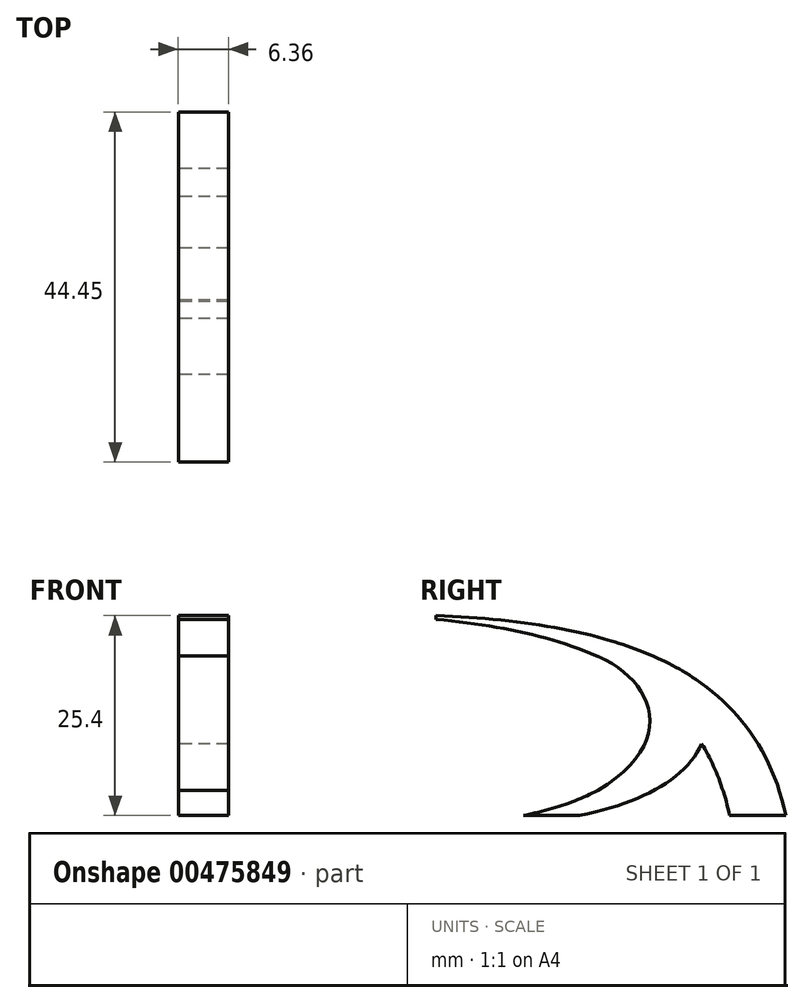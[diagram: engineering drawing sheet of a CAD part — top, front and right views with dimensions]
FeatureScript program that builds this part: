
annotation { "Feature Type Name" : "Feature", "Feature Type Description" : "" }
export const myFeature = defineFeature(function(context is Context, id is Id, definition is map)
    precondition{}
    {
        {
            var Q0;
            Q0=qCreatedBy(makeId("Right.planeOp"),FACE);
            var sketch = newSketch(context, id + "F0", { "sketchPlane" : qUnion([Q0])});
            skFitSpline(sketch, "E0", {"points": [v(226.4, -123.17) * mm, v(-307, 181.63) * mm], "startDerivative": vector(-152.15, 697.22) * mm, "endDerivative": vector(-800.1, 34.28) * mm});
            skFitSpline(sketch, "E1", {"points": [v(-40.3, 143.24) * mm, v(-173.65, -123.17) * mm], "startDerivative": vector(386.18, -408.72) * mm, "endDerivative": vector(-505.78, -101) * mm});
            skFitSpline(sketch, "E2", {"points": [v(45.43, 143.24) * mm, v(-87.92, -123.17) * mm], "startDerivative": vector(386.18, -408.72) * mm, "endDerivative": vector(-505.78, -101) * mm});
            skFitSpline(sketch, "E3", {"points": [v(140.68, -123.17) * mm, v(-392.72, 181.63) * mm], "startDerivative": vector(-152.15, 697.22) * mm, "endDerivative": vector(-800.1, 34.28) * mm});
            skFitSpline(sketch, "E4", {"points": [v(-62.31, 120.1) * mm, v(-60.29, -84.74) * mm], "startDerivative": vector(258.37, -104.87) * mm, "endDerivative": vector(-378.53, -222.19) * mm});
            skLineSegment(sketch, "E5", {"start": v(-307, 181.63) * mm, "end": v(-307, 175.93) * mm});
            skLineSegment(sketch, "E6", {"start": v(-173.65, -123.17) * mm, "end": v(-87.92, -123.17) * mm});
            skLineSegment(sketch, "E7", {"start": v(140.68, -123.17) * mm, "end": v(226.4, -123.17) * mm});
            skSolve(sketch);
        }
        {
            var Q0;
            {var subQ0=sQuery(id+"F0.wireOp",EDGE,"E1");var subQ1=sQuery(id+"F0.wireOp",EDGE,"E0");var subQ2=makeQuery(id+"F0.imprint","INTERSECT",VERTEX,{"derivedFrom":[subQ1,subQ0]});Q0=makeQuery(id+"F0.imprint","IMPRINT",FACE,{"disambiguationData":[TD([[makeQuery(id+"F0.imprint","IMPRINT",EDGE,{"disambiguationData":[TD([[subQ2,1.0]])],"derivedFrom":subQ1}),1.0]])]});}
            var Q1;
            {var subQ0=sQuery(id+"F0.wireOp",EDGE,"E7");Q1=makeQuery(id+"F0.imprint","IMPRINT",FACE,{"disambiguationData":[TD([[makeQuery(id+"F0.imprint","IMPRINT",EDGE,{"derivedFrom":subQ0}),1.0]])]});}
            var Q2;
            {var subQ8=sQuery(id+"F0.wireOp",EDGE,"E5");Q2=makeQuery(id+"F0.imprint","IMPRINT",FACE,{"disambiguationData":[TD([[makeQuery(id+"F0.imprint","IMPRINT",EDGE,{"derivedFrom":subQ8}),1.0]])]});}
            var Q3;
            {var subQ0=sQuery(id+"F0.wireOp",EDGE,"E4");var subQ1=sQuery(id+"F0.wireOp",EDGE,"E1");var subQ2=makeQuery(id+"F0.imprint","INTERSECT",VERTEX,{"derivedFrom":[subQ1,subQ0]});Q3=makeQuery(id+"F0.imprint","IMPRINT",FACE,{"disambiguationData":[TD([[makeQuery(id+"F0.imprint","IMPRINT",EDGE,{"disambiguationData":[TD([[subQ2,1.0]])],"derivedFrom":subQ1}),-1.0]])]});}
            var Q4;
            {var subQ0=sQuery(id+"F0.wireOp",EDGE,"E6");Q4=makeQuery(id+"F0.imprint","IMPRINT",FACE,{"disambiguationData":[TD([[makeQuery(id+"F0.imprint","IMPRINT",EDGE,{"derivedFrom":subQ0}),1.0]])]});}
            extrude(context, id + "F1", {"entities" : qUnion([Q0, Q1, Q2, Q3, Q4]), "depth" : 38.1 * mm, "hasSecondDirection" : true, "secondDirectionOppositeDirection" : true, "secondDirectionDepth" : 38.1 * mm});
        }
        {
            var Q0;
            Q0=makeQuery(id+"F1.opExtrude","SWEPT_BODY",BODY,{"disambiguationData":[OSD([sQuery(id+"F0.wireOp",EDGE,"E0"),sQuery(id+"F0.wireOp",EDGE,"E1"),sQuery(id+"F0.wireOp",EDGE,"E2"),sQuery(id+"F0.wireOp",EDGE,"E3"),sQuery(id+"F0.wireOp",EDGE,"E4"),sQuery(id+"F0.wireOp",EDGE,"E5"),sQuery(id+"F0.wireOp",EDGE,"E6"),sQuery(id+"F0.wireOp",EDGE,"E7")])]});
            var Q1;
            Q1=qCreatedBy(makeId("Origin.pointOp"),VERTEX);
            transform(context, id + "F2", {"entities" : qUnion([Q0]), "transformType" : TransformType.SCALE_UNIFORMLY, "scale" : 1 / 12, "scalePoint" : qUnion([Q1]), "makeCopy" : false});
        }
    });
